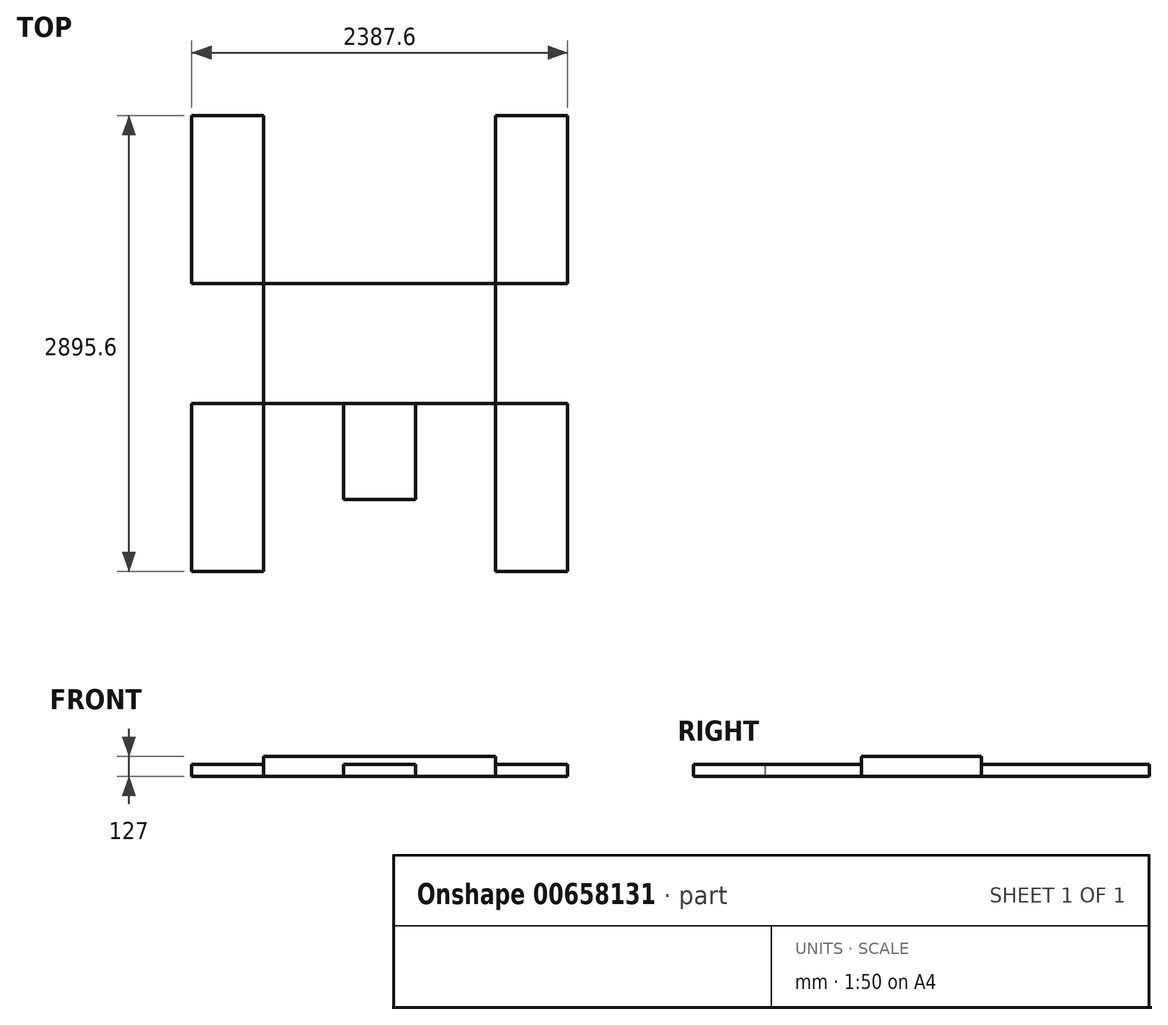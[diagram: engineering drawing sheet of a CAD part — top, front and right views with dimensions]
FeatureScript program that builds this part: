
annotation { "Feature Type Name" : "Feature", "Feature Type Description" : "" }
export const myFeature = defineFeature(function(context is Context, id is Id, definition is map)
    precondition{}
    {
        {
            var Q0;
            Q0=qCreatedBy(makeId("Top.planeOp"),FACE);
            var sketch = newSketch(context, id + "F0", { "sketchPlane" : qUnion([Q0])});
            skLineSegment(sketch, "E0.bottom", {"start": v(0, 0) * mm, "end": v(1473.2, 0) * mm});
            skLineSegment(sketch, "E0.top", {"start": v(0, 762) * mm, "end": v(1473.2, 762) * mm});
            skLineSegment(sketch, "E0.left", {"start": v(0, 0) * mm, "end": v(0, 762) * mm});
            skLineSegment(sketch, "E0.right", {"start": v(1473.2, 0) * mm, "end": v(1473.2, 762) * mm});
            skSolve(sketch);
        }
        {
            var Q0;
            Q0 = qSketchRegion(id + "F0", true);
            extrude(context, id + "F1", {"entities" : qUnion([Q0]), "depth" : 127 * mm, "offsetDistance" : 25.4 * mm});
        }
        {
            var Q0;
            Q0=makeQuery(id+"F1.opExtrude","CAP_FACE",FACE,{"disambiguationData":[OSD([sQuery(id+"F0.wireOp",EDGE,"E0.bottom"),sQuery(id+"F0.wireOp",EDGE,"E0.top"),sQuery(id+"F0.wireOp",EDGE,"E0.left"),sQuery(id+"F0.wireOp",EDGE,"E0.right")])],"isStart":false});
            var sketch = newSketch(context, id + "F2", { "sketchPlane" : qUnion([Q0])});
            skLineSegment(sketch, "E1.bottom", {"start": v(1473.2, 762) * mm, "end": v(1930.4, 762) * mm});
            skLineSegment(sketch, "E1.top", {"start": v(1473.2, 1828.8) * mm, "end": v(1930.4, 1828.8) * mm});
            skLineSegment(sketch, "E1.left", {"start": v(1473.2, 762) * mm, "end": v(1473.2, 1828.8) * mm});
            skLineSegment(sketch, "E1.right", {"start": v(1930.4, 762) * mm, "end": v(1930.4, 1828.8) * mm});
            skLineSegment(sketch, "E2.bottom", {"start": v(0, 762) * mm, "end": v(-457.2, 762) * mm});
            skLineSegment(sketch, "E2.top", {"start": v(0, 1828.8) * mm, "end": v(-457.2, 1828.8) * mm});
            skLineSegment(sketch, "E2.left", {"start": v(0, 762) * mm, "end": v(0, 1828.8) * mm});
            skLineSegment(sketch, "E2.right", {"start": v(-457.2, 762) * mm, "end": v(-457.2, 1828.8) * mm});
            skLineSegment(sketch, "E3.bottom", {"start": v(0, 0) * mm, "end": v(-457.2, 0) * mm});
            skLineSegment(sketch, "E3.top", {"start": v(0, -1066.8) * mm, "end": v(-457.2, -1066.8) * mm});
            skLineSegment(sketch, "E3.left", {"start": v(0, 0) * mm, "end": v(0, -1066.8) * mm});
            skLineSegment(sketch, "E3.right", {"start": v(-457.2, 0) * mm, "end": v(-457.2, -1066.8) * mm});
            skLineSegment(sketch, "E4.bottom", {"start": v(1473.2, 0) * mm, "end": v(1930.4, 0) * mm});
            skLineSegment(sketch, "E4.top", {"start": v(1473.2, -1066.8) * mm, "end": v(1930.4, -1066.8) * mm});
            skLineSegment(sketch, "E4.left", {"start": v(1473.2, 0) * mm, "end": v(1473.2, -1066.8) * mm});
            skLineSegment(sketch, "E4.right", {"start": v(1930.4, 0) * mm, "end": v(1930.4, -1066.8) * mm});
            skSolve(sketch);
        }
        {
            var Q0;
            Q0 = qSketchRegion(id + "F2", true);
            extrude(context, id + "F3", {"entities" : qUnion([Q0]), "oppositeDirection" : true, "depth" : 127 * mm, "offsetDistance" : 25.4 * mm, "hasSecondDirection" : true, "secondDirectionOppositeDirection" : true, "secondDirectionDepth" : 50.8 * mm});
        }
        {
            var Q0;
            Q0=makeQuery(id+"F1.opExtrude","CAP_FACE",FACE,{"disambiguationData":[OSD([sQuery(id+"F0.wireOp",EDGE,"E0.bottom"),sQuery(id+"F0.wireOp",EDGE,"E0.top"),sQuery(id+"F0.wireOp",EDGE,"E0.left"),sQuery(id+"F0.wireOp",EDGE,"E0.right")])],"isStart":false});
            var sketch = newSketch(context, id + "F4", { "sketchPlane" : qUnion([Q0])});
            skPoint(sketch, "E5", {"position": v(736.6, 0) * mm});
            skPoint(sketch, "E6", {"position": v(508, 0) * mm});
            skLineSegment(sketch, "E7.bottom", {"start": v(508, 0) * mm, "end": v(965.2, 0) * mm});
            skLineSegment(sketch, "E7.top", {"start": v(508, -609.6) * mm, "end": v(965.2, -609.6) * mm});
            skLineSegment(sketch, "E7.left", {"start": v(508, 0) * mm, "end": v(508, -609.6) * mm});
            skLineSegment(sketch, "E7.right", {"start": v(965.2, 0) * mm, "end": v(965.2, -609.6) * mm});
            skSolve(sketch);
        }
        {
            var Q0;
            Q0 = qSketchRegion(id + "F4", true);
            extrude(context, id + "F5", {"entities" : qUnion([Q0]), "oppositeDirection" : true, "depth" : 127 * mm, "offsetDistance" : 25.4 * mm, "hasSecondDirection" : true, "secondDirectionOppositeDirection" : true, "secondDirectionDepth" : 50.8 * mm});
        }
    });
